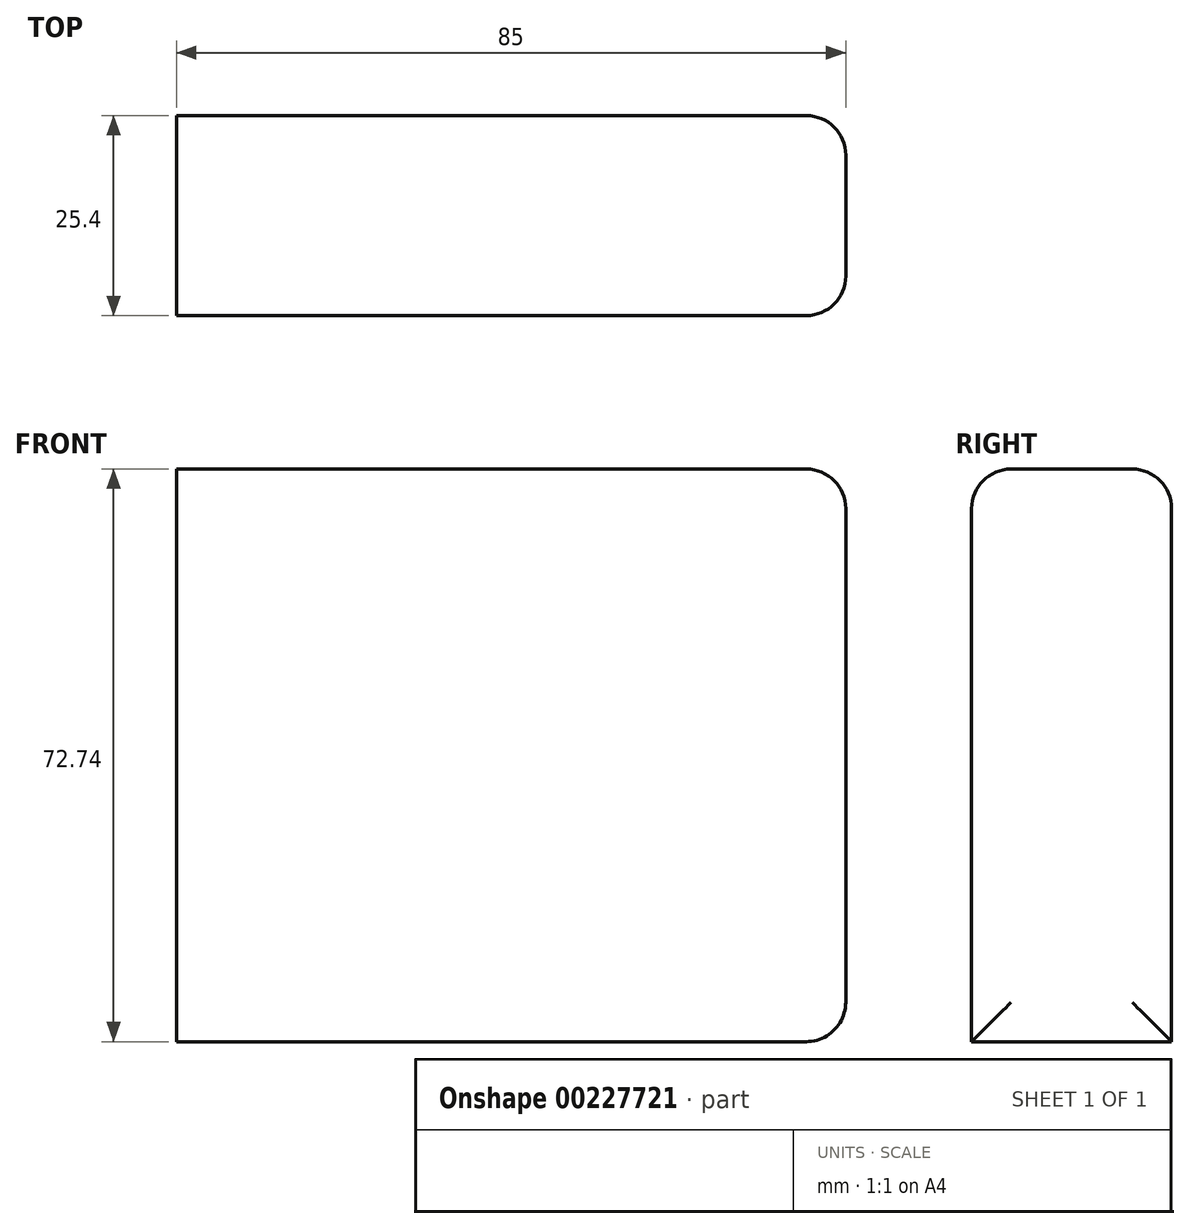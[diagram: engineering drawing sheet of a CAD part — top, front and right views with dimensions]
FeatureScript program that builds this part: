
annotation { "Feature Type Name" : "Feature", "Feature Type Description" : "" }
export const myFeature = defineFeature(function(context is Context, id is Id, definition is map)
    precondition{}
    {
        {
            var Q0;
            Q0=qCreatedBy(makeId("Front.planeOp"),FACE);
            var sketch = newSketch(context, id + "F0", { "sketchPlane" : qUnion([Q0])});
            skLineSegment(sketch, "E0.bottom", {"start": v(-59.04, 39.22) * mm, "end": v(25.96, 39.22) * mm});
            skLineSegment(sketch, "E0.top", {"start": v(-59.04, -33.52) * mm, "end": v(25.96, -33.52) * mm});
            skLineSegment(sketch, "E0.left", {"start": v(-59.04, 39.22) * mm, "end": v(-59.04, -33.52) * mm});
            skLineSegment(sketch, "E0.right", {"start": v(25.96, 39.22) * mm, "end": v(25.96, -33.52) * mm});
            skSolve(sketch);
        }
        {
            var Q0;
            Q0=makeQuery(id+"F0.imprint","IMPRINT",FACE,{"disambiguationData":[TD([[makeQuery(id+"F0.imprint","IMPRINT",EDGE,{"derivedFrom":sQuery(id+"F0.wireOp",EDGE,"E0.bottom")}),-1.0]])]});
            extrude(context, id + "F1", {"entities" : qUnion([Q0]), "depth" : 25.4 * mm});
        }
        {
            var Q0;
            Q0=makeQuery(id+"F1.opExtrude","SWEPT_EDGE",EDGE,{"disambiguationData":[OSD([sQuery(id+"F0.wireOp",EDGE,"E0.bottom"),sQuery(id+"F0.wireOp",EDGE,"E0.right")])]});
            fillet(context, id + "F2", {"entities" : qUnion([Q0]), "radius" : 5 * mm, "tangentPropagation" : true, "allowEdgeOverflow" : false});
        }
        {
            var Q0;
            Q0=makeQuery(id+"F1.opExtrude","SWEPT_FACE",FACE,{"disambiguationData":[OSD([sQuery(id+"F0.wireOp",EDGE,"E0.right")])]});
            var Q1;
            Q1=makeQuery(id+"F1.opExtrude","SWEPT_EDGE",EDGE,{"disambiguationData":[OSD([sQuery(id+"F0.wireOp",EDGE,"E0.bottom"),sQuery(id+"F0.wireOp",EDGE,"E0.right")])]});
            fillet(context, id + "F3", {"entities" : qUnion([Q0, Q1]), "radius" : 5 * mm, "tangentPropagation" : true, "allowEdgeOverflow" : false});
        }
    });
